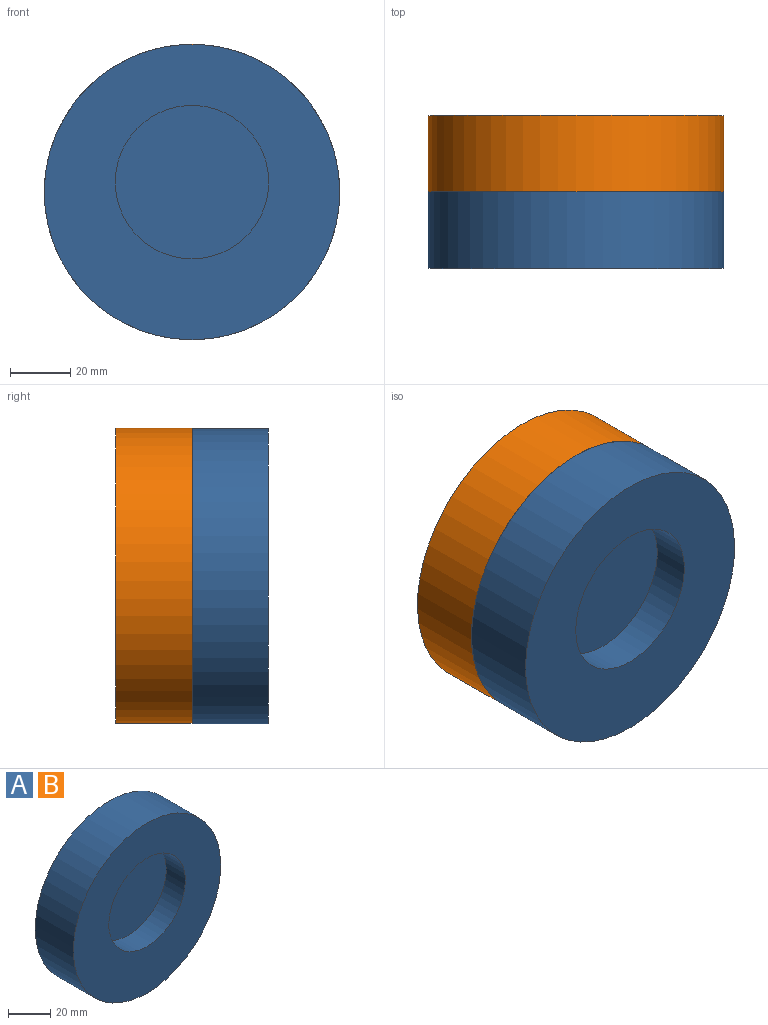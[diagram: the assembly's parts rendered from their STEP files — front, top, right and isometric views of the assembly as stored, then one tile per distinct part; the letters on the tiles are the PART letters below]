
ASSEMBLY  parts=2 mates=1
PART A: 5 faces, bbox 98.2x25.4x98.2 mm
  f0: cylinder r=49.09mm len=98.18mm, axis (0,1,0), area 7834.3mm2, adj f1,f2
  f1: plane 98.18x98.18mm, normal (0,-1,0), area 5528.7mm2, adj f0,f3
  f2: plane 98.18x98.18mm, normal (0,1,0), area 7570.5mm2, adj f0
  f3: cylinder r=25.49mm len=50.99mm, axis (0,-1,0), area 2034.3mm2, adj f1,f4
  f4: plane 50.99x50.99mm, normal (0,-1,0), area 2041.8mm2, adj f3
PART B: same geometry as A
PLACE A t=(-63.75,13.19,19.22)mm
PLACE B rot(axis=(1,0,0),180deg) t=(-63.75,13.19,19.22)mm
MATE fastened B.f0 <-> A.f0  axis (0,-1,0) through (-63.75,13.19,19.22)mm
